# Revit family: NLRS_57_AIR_UN_induction-unit-oknh600_LT_sacs
name_source: partatom
category: Mechanical Equipment
units: mm (PartAtom-declared; Revit-internal decimal feet)

## family parameters
Always vertical = Yes
Classification = None
Cut with Voids When Loaded = No
OmniClass Number = 23.75.00.00
OmniClass Title = Climate Control (HVAC)
Part Type = Normal
Room Calculation Point = No
Round Connector Dimension = Use Diameter
Shared = No
Work Plane-Based = No

## types (5) — shared parameters
Assembly Code = 57.00
Description = Induction unit, Type OKNH 600
FireRating = 00
IfcDescription = Induction unit, Type OKNH 600
IfcExportAs = IfcAirTerminalType
IfcExportType = DIFFUSER
LoadBearing = No
Manufacturer = Solid Air Climate Solutions
Model = Solid Air Induction Unit OKNH 600
NLRS_C_content_datum_uitgifte = 02-06-2023
NLRS_C_content_provider = Solid Air Climate Solutions
NLRS_C_content_versie = 3.20.01
SACS_Dummy = 1
SACS_Real_Width = 595 mm  [stored 1.9521 ft]
Type Comments = Do not mirror the model!
URL = https://solid-air.nl
zero-valued in all types: Default Elevation

## per-type parameters (varying)
| type | SACS_Base_Index | SACS_Height1 | SACS_Length_STD | SACS_Length_X2 | SACS_Plenum_L | SACS_Plenum_Offset |
| 600-1200 | 1 | 265 mm  [stored 0.869423 ft] | 1195 mm  [stored 3.9206 ft] | 1195 mm  [stored 3.9206 ft] | 1100 mm | 602 mm  [stored 1.97507 ft] |
| 600-1500 | 2 | 265 mm  [stored 0.869423 ft] | 1495 mm | 1495 mm | 1400 mm  [stored 4.59318 ft] | 752 mm  [stored 2.46719 ft] |
| 600-1800 | 3 | 265 mm  [stored 0.869423 ft] | 1795 mm | 1795 mm | 1700 mm  [stored 5.57743 ft] | 902 mm  [stored 2.95932 ft] |
| 600-2400 | 4 | 300 mm | 2395 mm  [stored 7.85761 ft] | 2395 mm  [stored 7.85761 ft] | 2300 mm | 1202 mm  [stored 3.94357 ft] |
| 600-3000 | 5 | 340 mm  [stored 1.11549 ft] | 2995 mm  [stored 9.82612 ft] | 2995 mm  [stored 9.82612 ft] | 2900 mm  [stored 9.51444 ft] | 1502 mm  [stored 4.92782 ft] |

note: [stored X ft] marks values corroborated as IEEE doubles in the binary element streams (Revit-internal decimal feet)

## geometry (parser evidence)
native form markers: Sweep x13
no freeform markers — native parametric forms only
